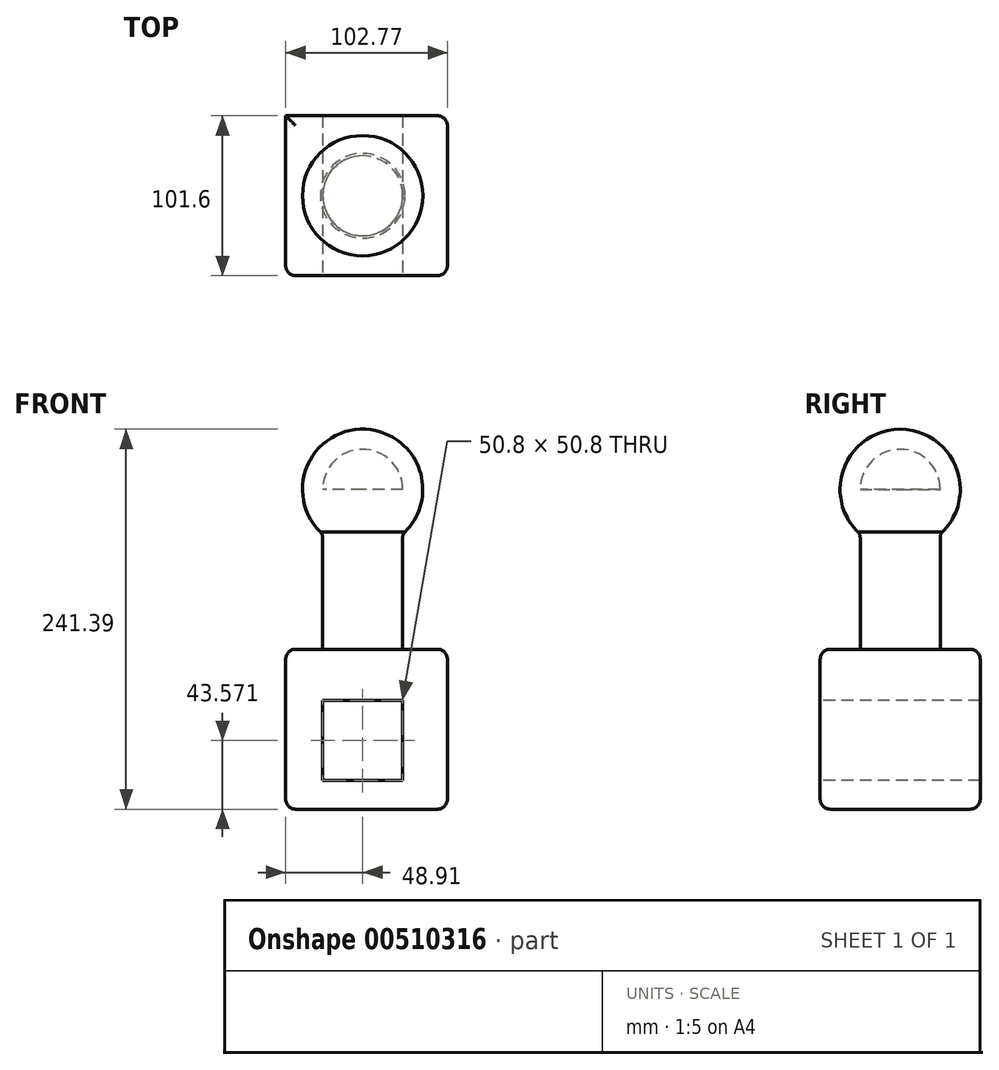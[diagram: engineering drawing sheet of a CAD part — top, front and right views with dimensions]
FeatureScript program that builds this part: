
annotation { "Feature Type Name" : "Feature", "Feature Type Description" : "" }
export const myFeature = defineFeature(function(context is Context, id is Id, definition is map)
    precondition{}
    {
        {
            var Q0;
            Q0=qCreatedBy(makeId("Top.planeOp"),FACE);
            var sketch = newSketch(context, id + "F0", { "sketchPlane" : qUnion([Q0])});
            skLineSegment(sketch, "E0.bottom", {"start": v(-48.9, -50.8) * mm, "end": v(53.86, -50.8) * mm});
            skLineSegment(sketch, "E0.top", {"start": v(-48.9, 50.8) * mm, "end": v(53.86, 50.8) * mm});
            skLineSegment(sketch, "E0.left", {"start": v(-48.9, -50.8) * mm, "end": v(-48.9, 50.8) * mm});
            skLineSegment(sketch, "E0.right", {"start": v(53.86, -50.8) * mm, "end": v(53.86, 50.8) * mm});
            skPoint(sketch, "E0.middle", {"position": v(2.48, 0) * mm});
            skSolve(sketch);
        }
        {
            var Q0;
            Q0 = qSketchRegion(id + "F0", true);
            extrude(context, id + "F1", {"entities" : qUnion([Q0]), "depth" : 101.6 * mm, "offsetDistance" : 25.4 * mm});
        }
        {
            var Q0;
            Q0=makeQuery(id+"F1.opExtrude","CAP_FACE",FACE,{"disambiguationData":[OSD([sQuery(id+"F0.wireOp",EDGE,"E0.bottom"),sQuery(id+"F0.wireOp",EDGE,"E0.top"),sQuery(id+"F0.wireOp",EDGE,"E0.left"),sQuery(id+"F0.wireOp",EDGE,"E0.right")])],"isStart":false});
            var sketch = newSketch(context, id + "F2", { "sketchPlane" : qUnion([Q0])});
            skCircle(sketch, "E1", {"center": v(0, 0) * mm, "radius": 25.4 * mm});
            skSolve(sketch);
        }
        {
            var Q0;
            Q0=makeQuery(id+"F2.imprint","IMPRINT",FACE,{"disambiguationData":[TD([[makeQuery(id+"F2.imprint","IMPRINT",EDGE,{"derivedFrom":sQuery(id+"F2.wireOp",EDGE,"E1")}),1.0]])]});
            extrude(context, id + "F3", {"entities" : qUnion([Q0]), "operationType" : NewBodyOperationType.ADD, "depth" : 101.6 * mm, "offsetDistance" : 25.4 * mm});
        }
        {
            var Q0;
            Q0=makeQuery(id+"F3.opExtrude","CAP_FACE",FACE,{"disambiguationData":[OSD([sQuery(id+"F2.wireOp",EDGE,"E1")])],"isStart":false});
            var sketch = newSketch(context, id + "F4", { "sketchPlane" : qUnion([Q0])});
            skCircle(sketch, "E2", {"center": v(0, 0) * mm, "radius": 38.19 * mm});
            skLineSegment(sketch, "E3", {"start": v(0, 38.19) * mm, "end": v(0, -40.7) * mm});
            skSolve(sketch);
        }
        {
            var Q0;
            {var subQ0=sQuery(id+"F4.wireOp",EDGE,"E3");var subQ1=sQuery(id+"F4.wireOp",EDGE,"E2");var subQ2=makeQuery(id+"F4.imprint","INTERSECT",VERTEX,{"disambiguationData":[OD(0.0)],"derivedFrom":[subQ1,subQ0]});Q0=makeQuery(id+"F4.imprint","IMPRINT",FACE,{"disambiguationData":[TD([[makeQuery(id+"F4.imprint","IMPRINT",EDGE,{"disambiguationData":[TD([[subQ2,1.0]])],"derivedFrom":subQ1}),1.0]])]});}
            var Q1;
            Q1=sQuery(id+"F4.wireOp",EDGE,"E3");
            revolve(context, id + "F5", {"operationType" : NewBodyOperationType.ADD, "entities" : qUnion([Q0]), "axis" : qUnion([Q1]), "revolveType" : RevolveType.FULL});
        }
        {
            var Q0;
            Q0=makeQuery(id+"F1.opExtrude","SWEPT_FACE",FACE,{"disambiguationData":[OSD([sQuery(id+"F0.wireOp",EDGE,"E0.bottom")])]});
            var sketch = newSketch(context, id + "F6", { "sketchPlane" : qUnion([Q0])});
            skLineSegment(sketch, "E4.bottom", {"start": v(-25.4, 68.97) * mm, "end": v(25.4, 68.97) * mm});
            skLineSegment(sketch, "E4.top", {"start": v(-25.4, 18.17) * mm, "end": v(25.4, 18.17) * mm});
            skLineSegment(sketch, "E4.left", {"start": v(-25.4, 68.97) * mm, "end": v(-25.4, 18.17) * mm});
            skLineSegment(sketch, "E4.right", {"start": v(25.4, 68.97) * mm, "end": v(25.4, 18.17) * mm});
            skPoint(sketch, "E4.middle", {"position": v(0, 43.57) * mm});
            skSolve(sketch);
        }
        {
            var Q0;
            Q0=makeQuery(id+"F6.imprint","IMPRINT",FACE,{"disambiguationData":[TD([[makeQuery(id+"F6.imprint","IMPRINT",EDGE,{"derivedFrom":sQuery(id+"F6.wireOp",EDGE,"E4.bottom")}),-1.0]])]});
            extrude(context, id + "F7", {"entities" : qUnion([Q0]), "operationType" : NewBodyOperationType.REMOVE, "oppositeDirection" : true, "depth" : 101.6 * mm, "offsetDistance" : 25.4 * mm});
        }
        {
            var Q0;
            Q0=makeQuery(id+"F1.opExtrude","CAP_EDGE",EDGE,{"disambiguationData":[OSD([sQuery(id+"F0.wireOp",EDGE,"E0.right")])],"isStart":false});
            var Q1;
            Q1=makeQuery(id+"F1.opExtrude","SWEPT_EDGE",EDGE,{"disambiguationData":[OSD([sQuery(id+"F0.wireOp",EDGE,"E0.bottom"),sQuery(id+"F0.wireOp",EDGE,"E0.right")])]});
            var Q2;
            Q2=makeQuery(id+"F1.opExtrude","SWEPT_EDGE",EDGE,{"disambiguationData":[OSD([sQuery(id+"F0.wireOp",EDGE,"E0.top"),sQuery(id+"F0.wireOp",EDGE,"E0.right")])]});
            var Q3;
            Q3=makeQuery(id+"F1.opExtrude","CAP_EDGE",EDGE,{"disambiguationData":[OSD([sQuery(id+"F0.wireOp",EDGE,"E0.right")])],"isStart":true});
            var Q4;
            Q4=makeQuery(id+"F1.opExtrude","CAP_EDGE",EDGE,{"disambiguationData":[OSD([sQuery(id+"F0.wireOp",EDGE,"E0.bottom")])],"isStart":false});
            var Q5;
            Q5=makeQuery(id+"F1.opExtrude","SWEPT_EDGE",EDGE,{"disambiguationData":[OSD([sQuery(id+"F0.wireOp",EDGE,"E0.bottom"),sQuery(id+"F0.wireOp",EDGE,"E0.left")])]});
            var Q6;
            Q6=makeQuery(id+"F1.opExtrude","CAP_EDGE",EDGE,{"disambiguationData":[OSD([sQuery(id+"F0.wireOp",EDGE,"E0.left")])],"isStart":false});
            var Q7;
            Q7=makeQuery(id+"F1.opExtrude","CAP_EDGE",EDGE,{"disambiguationData":[OSD([sQuery(id+"F0.wireOp",EDGE,"E0.top")])],"isStart":false});
            var Q8;
            Q8=makeQuery(id+"F1.opExtrude","CAP_EDGE",EDGE,{"disambiguationData":[OSD([sQuery(id+"F0.wireOp",EDGE,"E0.bottom")])],"isStart":true});
            var Q9;
            Q9=makeQuery(id+"F1.opExtrude","CAP_EDGE",EDGE,{"disambiguationData":[OSD([sQuery(id+"F0.wireOp",EDGE,"E0.left")])],"isStart":true});
            var Q10;
            Q10=makeQuery(id+"F1.opExtrude","CAP_EDGE",EDGE,{"disambiguationData":[OSD([sQuery(id+"F0.wireOp",EDGE,"E0.top")])],"isStart":true});
            fillet(context, id + "F8", {"entities" : qUnion([Q0, Q1, Q2, Q3, Q4, Q5, Q6, Q7, Q8, Q9, Q10]), "radius" : 6.35 * mm, "tangentPropagation" : true, "allowEdgeOverflow" : false});
        }
        {
            var Q0;
            Q0=makeQuery(id+"F3.opExtrude","CAP_EDGE",EDGE,{"disambiguationData":[OSD([sQuery(id+"F2.wireOp",EDGE,"E1")])],"isStart":true});
            var Q1;
            Q1=makeQuery(id+"F5.boolean.opBoolean","INTERSECT",EDGE,{"derivedFrom":[makeQuery(id+"F3.opExtrude","SWEPT_FACE",FACE,{"disambiguationData":[OSD([sQuery(id+"F2.wireOp",EDGE,"E1")])]}),makeQuery(id+"F5.opRevolve","SWEPT_FACE",FACE,{"disambiguationData":[OSD([sQuery(id+"F4.wireOp",EDGE,"E2")])]})]});
            fillet(context, id + "F9", {"entities" : qUnion([Q0, Q1]), "radius" : 5.08 * mm, "tangentPropagation" : true, "allowEdgeOverflow" : false});
        }
    });
